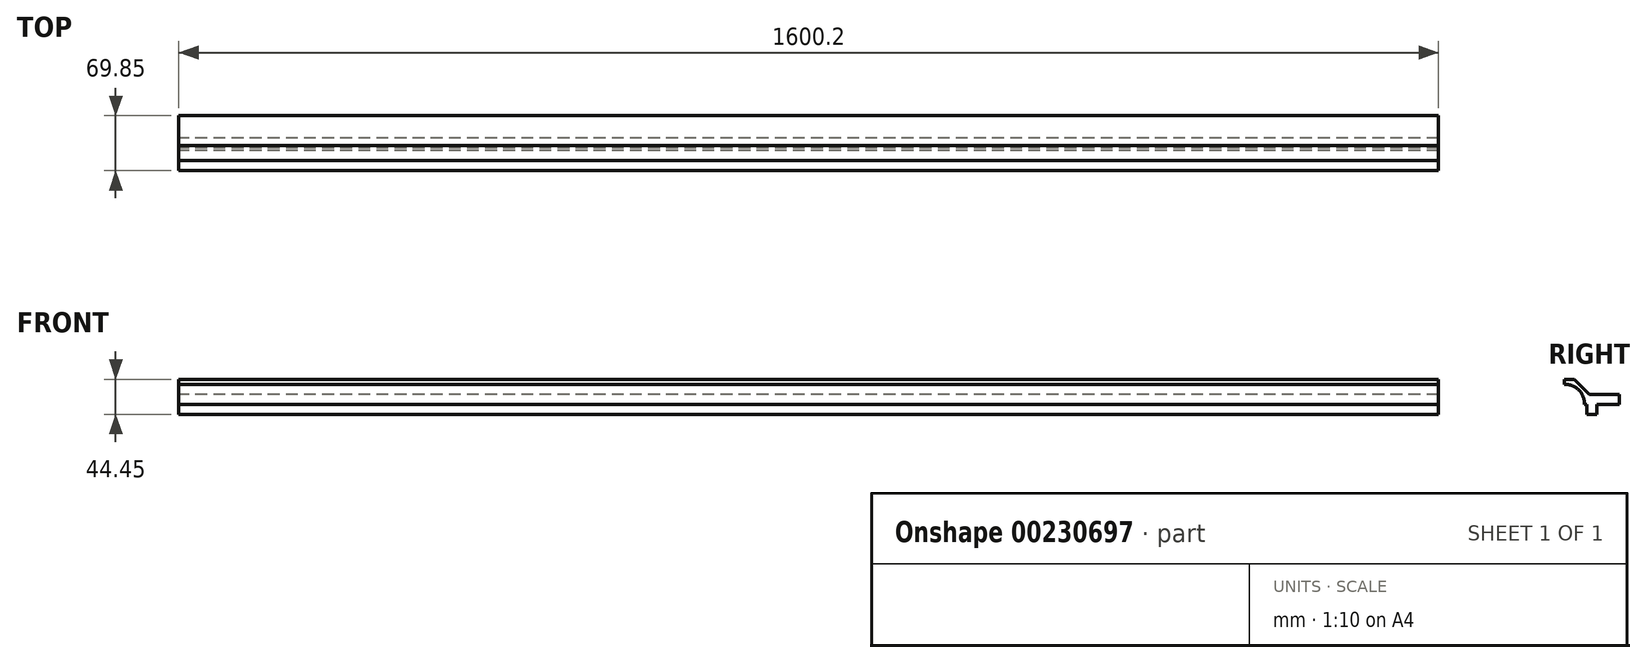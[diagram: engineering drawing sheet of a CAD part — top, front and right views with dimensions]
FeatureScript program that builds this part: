
annotation { "Feature Type Name" : "Feature", "Feature Type Description" : "" }
export const myFeature = defineFeature(function(context is Context, id is Id, definition is map)
    precondition{}
    {
        {
            var Q0;
            Q0=qCreatedBy(makeId("Right.planeOp"),FACE);
            var sketch = newSketch(context, id + "F0", { "sketchPlane" : qUnion([Q0])});
            skLineSegment(sketch, "E0", {"start": v(-32, 17.89) * mm, "end": v(-32, 24.24) * mm});
            skLineSegment(sketch, "E1", {"start": v(-32, 24.24) * mm, "end": v(-19.3, 24.24) * mm});
            skLineSegment(sketch, "E2", {"start": v(-19.3, 24.24) * mm, "end": v(-0.26, 5.19) * mm});
            skLineSegment(sketch, "E3", {"start": v(-0.26, 5.19) * mm, "end": v(-0.26, -7.51) * mm});
            skLineSegment(sketch, "E4", {"start": v(-0.26, -7.51) * mm, "end": v(-6.6, -7.51) * mm});
            skArc(sketch, "E5", {"start": v(-6.6, -7.51) * mm, "mid": v(-13.85, 10.64) * mm, "end": v(-32, 17.89) * mm});
            skLineSegment(sketch, "E6.bottom", {"start": v(-0.26, 5.19) * mm, "end": v(37.84, 5.19) * mm});
            skLineSegment(sketch, "E6.top", {"start": v(-0.26, -7.51) * mm, "end": v(37.84, -7.51) * mm});
            skLineSegment(sketch, "E6.right", {"start": v(37.84, 5.19) * mm, "end": v(37.84, -7.51) * mm});
            skLineSegment(sketch, "E7.bottom", {"start": v(-3.43, -7.51) * mm, "end": v(9.27, -7.51) * mm});
            skLineSegment(sketch, "E7.top", {"start": v(-3.43, -20.21) * mm, "end": v(9.27, -20.21) * mm});
            skLineSegment(sketch, "E7.left", {"start": v(-3.43, -7.51) * mm, "end": v(-3.43, -20.21) * mm});
            skLineSegment(sketch, "E7.right", {"start": v(9.27, -7.51) * mm, "end": v(9.27, -20.21) * mm});
            skSolve(sketch);
        }
        {
            var Q0;
            Q0=makeQuery(id+"F0.imprint","IMPRINT",FACE,{"disambiguationData":[TD([[makeQuery(id+"F0.imprint","IMPRINT",EDGE,{"derivedFrom":sQuery(id+"F0.wireOp",EDGE,"E0")}),-1.0]])]});
            var Q1;
            Q1=makeQuery(id+"F0.imprint","IMPRINT",FACE,{"disambiguationData":[TD([[makeQuery(id+"F0.imprint","IMPRINT",EDGE,{"derivedFrom":sQuery(id+"F0.wireOp",EDGE,"E6.bottom")}),-1.0]])]});
            var Q2;
            Q2=makeQuery(id+"F0.imprint","IMPRINT",FACE,{"disambiguationData":[TD([[makeQuery(id+"F0.imprint","IMPRINT",EDGE,{"derivedFrom":sQuery(id+"F0.wireOp",EDGE,"E7.top")}),1.0]])]});
            extrude(context, id + "F1", {"entities" : qUnion([Q0, Q1, Q2]), "depth" : 1600.2 * mm});
        }
    });
